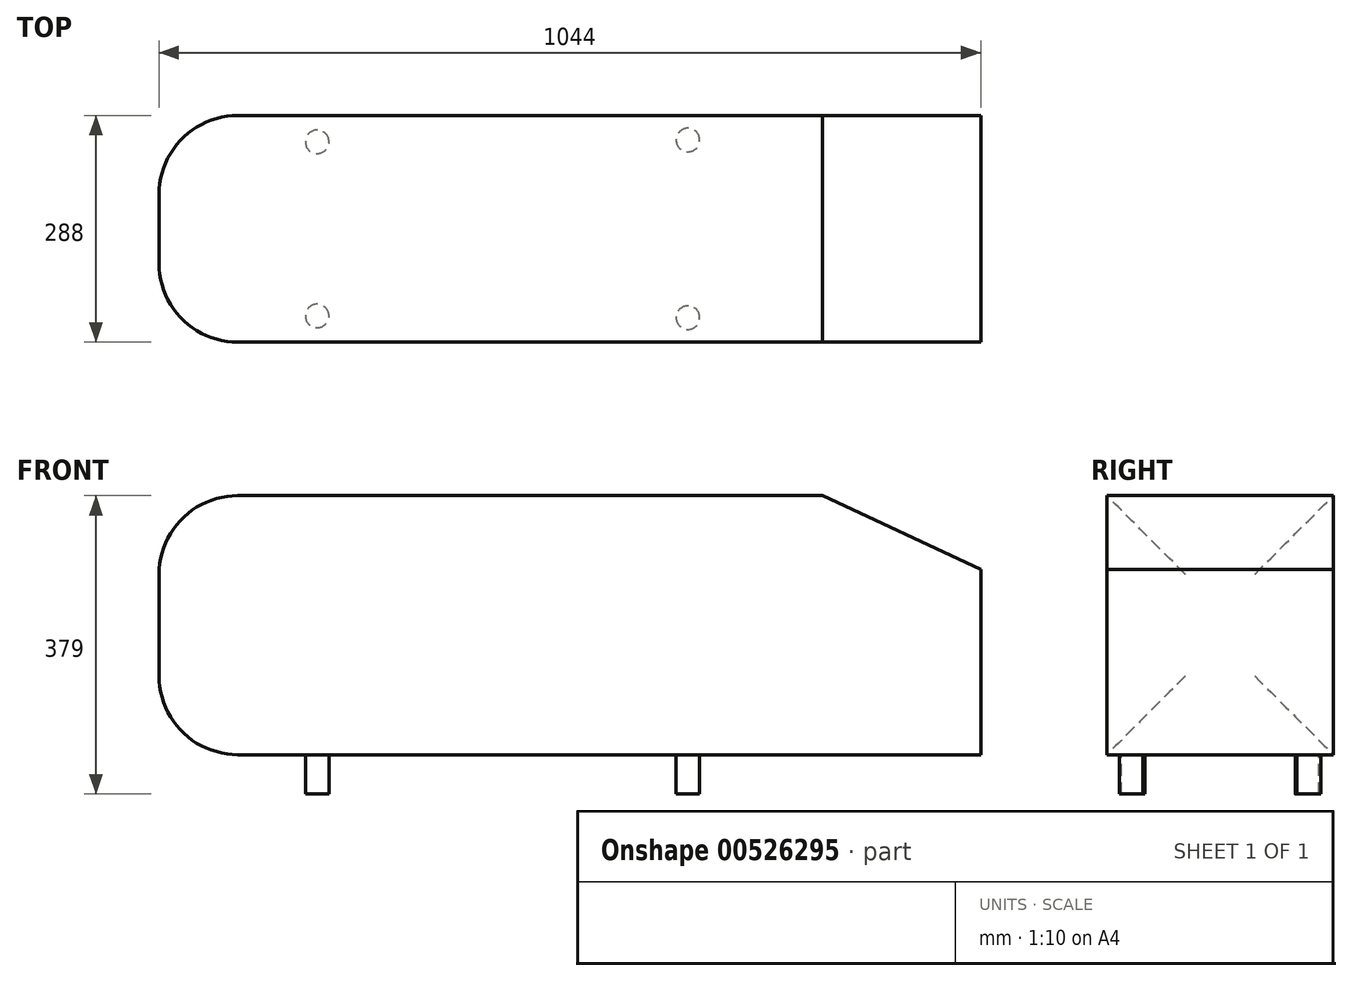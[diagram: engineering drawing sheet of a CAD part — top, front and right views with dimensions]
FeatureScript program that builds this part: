
annotation { "Feature Type Name" : "Feature", "Feature Type Description" : "" }
export const myFeature = defineFeature(function(context is Context, id is Id, definition is map)
    precondition{}
    {
        {
            var Q0;
            Q0=qCreatedBy(makeId("Front.planeOp"),FACE);
            var sketch = newSketch(context, id + "F0", { "sketchPlane" : qUnion([Q0])});
            skLineSegment(sketch, "E0.bottom", {"start": v(-525.76, 219.56) * mm, "end": v(518.24, 219.56) * mm});
            skLineSegment(sketch, "E0.top", {"start": v(-525.76, -109.44) * mm, "end": v(518.24, -109.44) * mm});
            skLineSegment(sketch, "E0.left", {"start": v(-525.76, 219.56) * mm, "end": v(-525.76, -109.44) * mm});
            skLineSegment(sketch, "E0.right", {"start": v(518.24, 219.56) * mm, "end": v(518.24, -109.44) * mm});
            skSolve(sketch);
        }
        {
            var Q0;
            Q0=makeQuery(id+"F0.imprint","IMPRINT",FACE,{"disambiguationData":[TD([[makeQuery(id+"F0.imprint","IMPRINT",EDGE,{"derivedFrom":sQuery(id+"F0.wireOp",EDGE,"E0.bottom")}),-1.0]])]});
            extrude(context, id + "F1", {"entities" : qUnion([Q0]), "oppositeDirection" : true, "depth" : 288 * mm, "offsetDistance" : 25 * mm});
        }
        {
            var Q0;
            Q0=makeQuery(id+"F1.opExtrude","SWEPT_FACE",FACE,{"disambiguationData":[OSD([sQuery(id+"F0.wireOp",EDGE,"E0.left")])]});
            fillet(context, id + "F2", {"entities" : qUnion([Q0]), "radius" : 100 * mm, "tangentPropagation" : true, "allowEdgeOverflow" : false});
        }
        {
            var Q0;
            Q0=makeQuery(id+"F1.opExtrude","CAP_FACE",FACE,{"disambiguationData":[OSD([sQuery(id+"F0.wireOp",EDGE,"E0.bottom"),sQuery(id+"F0.wireOp",EDGE,"E0.top"),sQuery(id+"F0.wireOp",EDGE,"E0.left"),sQuery(id+"F0.wireOp",EDGE,"E0.right")])],"isStart":true});
            var sketch = newSketch(context, id + "F3", { "sketchPlane" : qUnion([Q0])});
            skLineSegment(sketch, "E1", {"start": v(317.04, 219.56) * mm, "end": v(518.24, 125.74) * mm});
            skSolve(sketch);
        }
        {
            var Q0;
            Q0 = qSketchRegion(id + "F3", true);
            var Q1;
            {var subQ0=sQuery(id+"F3.wireOp",EDGE,"E1");Q1=makeQuery(id+"F3.imprint","IMPRINT",FACE,{"disambiguationData":[TD([[makeQuery(id+"F3.imprint","IMPRINT",EDGE,{"derivedFrom":subQ0}),1.0]])]});}
            extrude(context, id + "F4", {"entities" : qUnion([Q0, Q1]), "operationType" : NewBodyOperationType.REMOVE, "endBound" : BoundingType.THROUGH_ALL, "oppositeDirection" : true, "depth" : 25 * mm, "offsetDistance" : 25 * mm});
        }
        {
            var Q0;
            Q0=makeQuery(id+"F1.opExtrude","SWEPT_FACE",FACE,{"disambiguationData":[OSD([sQuery(id+"F0.wireOp",EDGE,"E0.top")])]});
            var sketch = newSketch(context, id + "F5", { "sketchPlane" : qUnion([Q0])});
            skCircle(sketch, "E2", {"center": v(-324.76, -33.37) * mm, "radius": 15 * mm});
            skCircle(sketch, "E3", {"center": v(146.24, -31.19) * mm, "radius": 15 * mm});
            skLineSegment(sketch, "E4", {"start": v(-425.76, -144) * mm, "end": v(518.24, -144) * mm, "construction": true});
            skCircle(sketch, "E5.MirrorC", {"center": v(-324.76, -254.63) * mm, "radius": 15 * mm});
            skCircle(sketch, "E6.MirrorC", {"center": v(146.24, -256.81) * mm, "radius": 15 * mm});
            skSolve(sketch);
        }
        {
            var Q0;
            Q0 = qSketchRegion(id + "F5", true);
            extrude(context, id + "F6", {"entities" : qUnion([Q0]), "operationType" : NewBodyOperationType.ADD, "depth" : 50 * mm, "offsetDistance" : 25 * mm});
        }
    });
